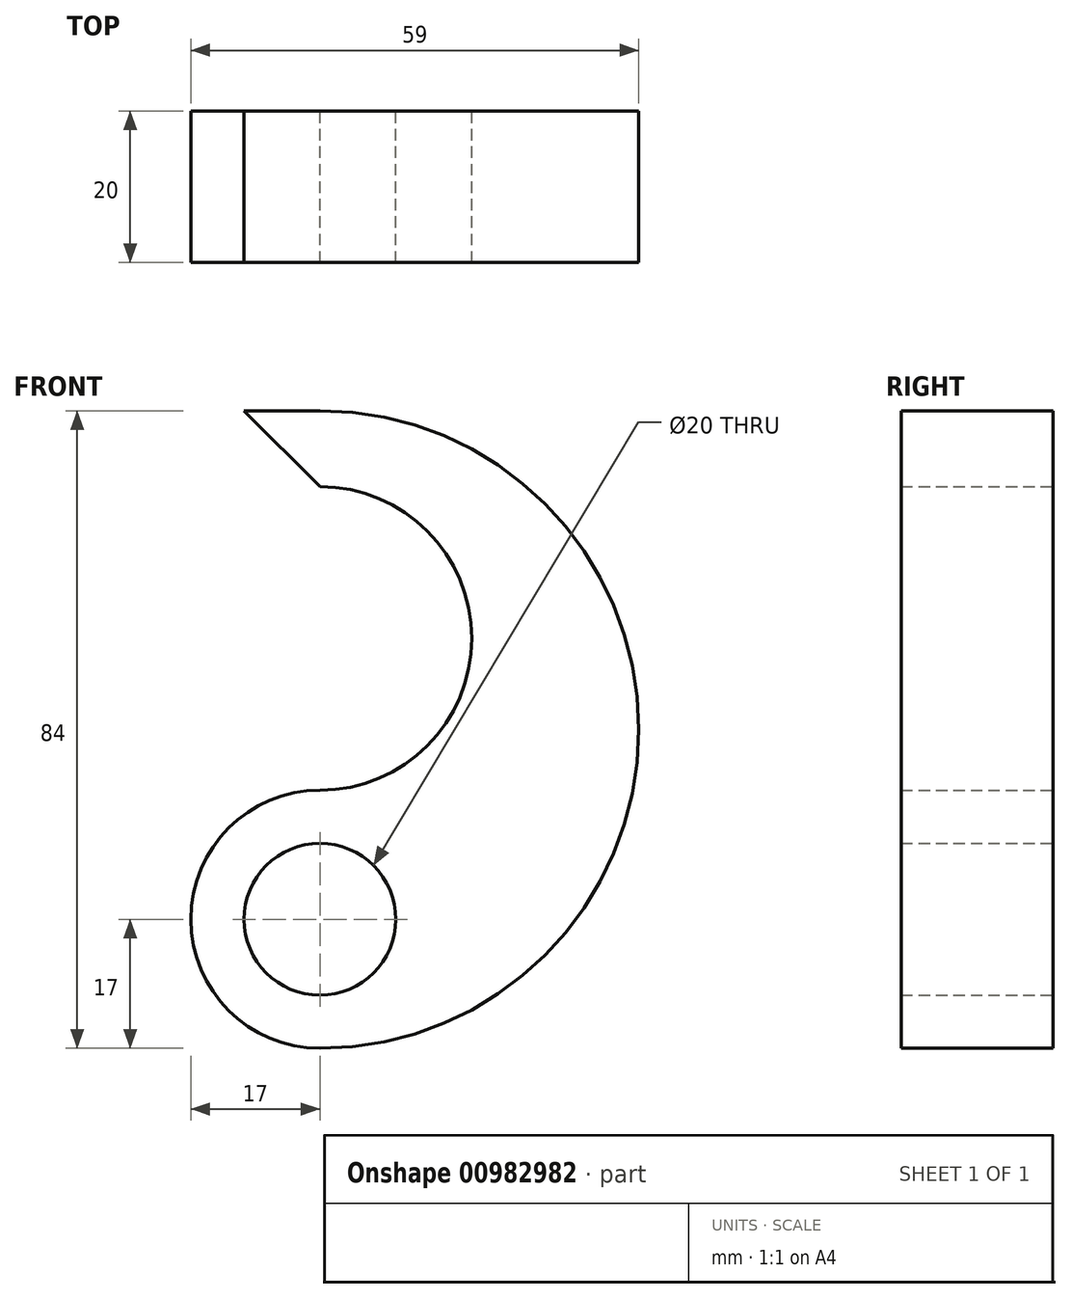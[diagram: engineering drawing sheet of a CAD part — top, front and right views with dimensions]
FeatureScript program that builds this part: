
annotation { "Feature Type Name" : "Feature", "Feature Type Description" : "" }
export const myFeature = defineFeature(function(context is Context, id is Id, definition is map)
    precondition{}
    {
        {
            var Q0;
            Q0=qCreatedBy(makeId("Front.planeOp"),FACE);
            var sketch = newSketch(context, id + "F0", { "sketchPlane" : qUnion([Q0])});
            skCircle(sketch, "E0", {"center": v(0, 0) * mm, "radius": 10 * mm});
            skArc(sketch, "E1", {"start": v(0, -17) * mm, "mid": v(42, 25) * mm, "end": v(0, 67) * mm});
            skArc(sketch, "E2", {"start": v(0, 17) * mm, "mid": v(20, 37) * mm, "end": v(0, 57) * mm});
            skArc(sketch, "E3", {"start": v(0, 17) * mm, "mid": v(-17, 0) * mm, "end": v(0, -17) * mm});
            skLineSegment(sketch, "E4", {"start": v(0, 57) * mm, "end": v(-10, 67) * mm});
            skLineSegment(sketch, "E5", {"start": v(-10, 67) * mm, "end": v(0, 67) * mm});
            skSolve(sketch);
        }
        {
            var Q0;
            Q0=makeQuery(id+"F0.imprint","IMPRINT",FACE,{"disambiguationData":[TD([[makeQuery(id+"F0.imprint","IMPRINT",EDGE,{"derivedFrom":sQuery(id+"F0.wireOp",EDGE,"E0")}),-1.0]])]});
            extrude(context, id + "F1", {"entities" : qUnion([Q0]), "endBound" : BoundingType.SYMMETRIC, "depth" : 20 * mm, "offsetDistance" : 25 * mm});
        }
    });
